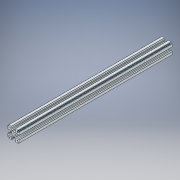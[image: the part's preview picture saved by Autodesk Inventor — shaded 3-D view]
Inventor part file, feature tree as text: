
AUTODESK INVENTOR PART (.ipt)
format: ipt  version: 2017 (Build 210142000, 142)  size: 297,472 bytes
history: native  units: in
note: dims shown in document units (in); Inventor stores cm internally (conversion verified against a paired STEP export)
features: extrude x1, sketch x1, fillet x1
ambient origin geometry x8: Origin, YZ Plane, XZ Plane, XY Plane, X Axis, Y Axis, Z Axis, Center Point
bodies: Solid1 (feature_tree)
feature tree (3):
  extrude  "Extrusion1"  [1 undecoded]
  sketch  "Sketch1"  dims[d0=59.0in d1=0.0in]
  fillet  "Fillet10"  [1 undecoded]
note: 2 required parameter values undecoded (feature->parameter linkage not recoverable at this tier; creation-order binding heuristic only, values carry confidence <= 0.55)
